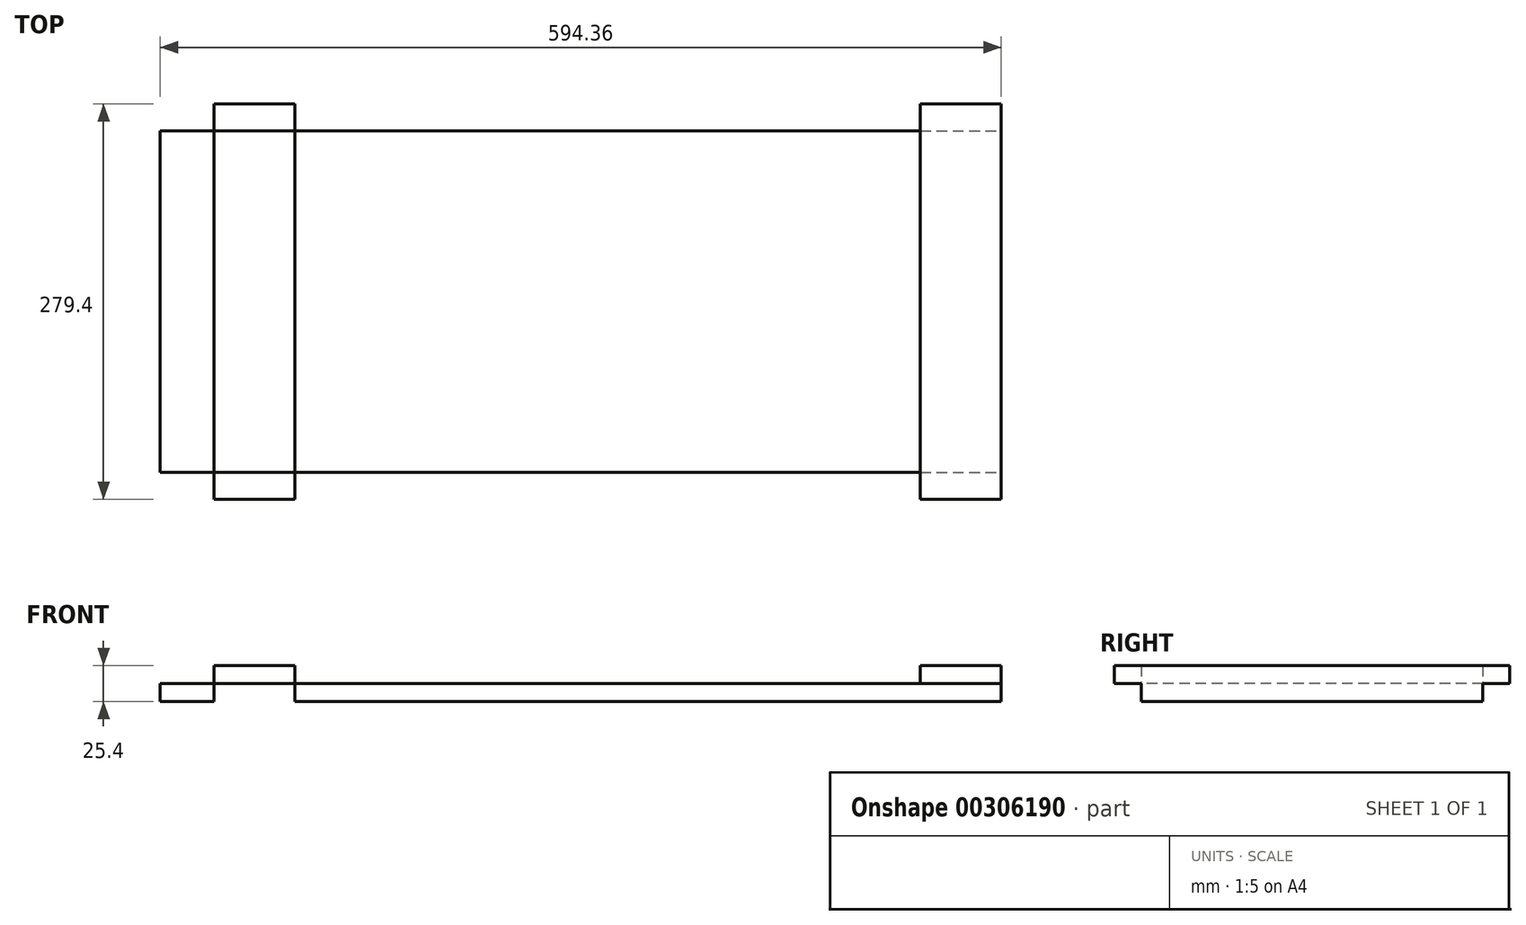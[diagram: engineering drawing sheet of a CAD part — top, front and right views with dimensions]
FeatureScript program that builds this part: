
annotation { "Feature Type Name" : "Feature", "Feature Type Description" : "" }
export const myFeature = defineFeature(function(context is Context, id is Id, definition is map)
    precondition{}
    {
        {
            var Q0;
            Q0=qCreatedBy(makeId("Top.planeOp"),FACE);
            var sketch = newSketch(context, id + "F0", { "sketchPlane" : qUnion([Q0])});
            skLineSegment(sketch, "E0.bottom", {"start": v(-297.18, 120.65) * mm, "end": v(297.18, 120.65) * mm});
            skLineSegment(sketch, "E0.top", {"start": v(-297.18, -120.65) * mm, "end": v(297.18, -120.65) * mm});
            skLineSegment(sketch, "E0.left", {"start": v(-297.18, 120.65) * mm, "end": v(-297.18, -120.65) * mm});
            skLineSegment(sketch, "E0.right", {"start": v(297.18, 120.65) * mm, "end": v(297.18, -120.65) * mm});
            skPoint(sketch, "E0.middle", {"position": v(0, 0) * mm});
            skLineSegment(sketch, "E1.bottom", {"start": v(-259.08, 139.7) * mm, "end": v(-201.93, 139.7) * mm});
            skLineSegment(sketch, "E1.top", {"start": v(-259.08, -139.7) * mm, "end": v(-201.93, -139.7) * mm});
            skLineSegment(sketch, "E1.left", {"start": v(-259.08, 139.7) * mm, "end": v(-259.08, -139.7) * mm});
            skLineSegment(sketch, "E1.right", {"start": v(-201.93, 139.7) * mm, "end": v(-201.93, -139.7) * mm});
            skLineSegment(sketch, "E2", {"start": v(-259.08, 120.65) * mm, "end": v(-201.93, 120.65) * mm});
            skLineSegment(sketch, "E3", {"start": v(-259.08, -120.65) * mm, "end": v(-201.93, -120.65) * mm});
            skLineSegment(sketch, "E4.bottom", {"start": v(297.18, 139.7) * mm, "end": v(240.03, 139.7) * mm});
            skLineSegment(sketch, "E4.top", {"start": v(297.18, -139.7) * mm, "end": v(240.03, -139.7) * mm});
            skLineSegment(sketch, "E4.left", {"start": v(297.18, 139.7) * mm, "end": v(297.18, -139.7) * mm});
            skLineSegment(sketch, "E4.right", {"start": v(240.03, 139.7) * mm, "end": v(240.03, -139.7) * mm});
            skSolve(sketch);
        }
        {
            var Q0;
            {var subQ0=sQuery(id+"F0.wireOp",EDGE,"E0.left");Q0=makeQuery(id+"F0.imprint","IMPRINT",FACE,{"disambiguationData":[TD([[makeQuery(id+"F0.imprint","IMPRINT",EDGE,{"derivedFrom":subQ0}),1.0]])]});}
            var Q1;
            Q1=makeQuery(id+"F0.imprint","IMPRINT",FACE,{"disambiguationData":[TD([[makeQuery(id+"F0.imprint","IMPRINT",EDGE,{"derivedFrom":sQuery(id+"F0.wireOp",EDGE,"ijQMFZE7-lGvI-Rrje-spdO-LlXZxQpasY5D.bottom")}),-1.0]])]});
            var Q2;
            {var subQ2=sQuery(id+"F0.wireOp",EDGE,"ijQMFZE7-lGvI-Rrje-spdO-LlXZxQpasY5D.right");Q2=makeQuery(id+"F0.imprint","IMPRINT",FACE,{"disambiguationData":[TD([[makeQuery(id+"F0.imprint","IMPRINT",EDGE,{"derivedFrom":subQ2}),1.0]])]});}
            var Q3;
            Q3=makeQuery(id+"F0.imprint","IMPRINT",FACE,{"disambiguationData":[TD([[makeQuery(id+"F0.imprint","IMPRINT",EDGE,{"derivedFrom":sQuery(id+"F0.wireOp",EDGE,"27S9jRhR-VNvc-t6gW-FhnJ-kzvBXy7unaTU.bottom")}),1.0]])]});
            var Q4;
            {var subQ0=sQuery(id+"F0.wireOp",EDGE,"E2");Q4=makeQuery(id+"F0.imprint","IMPRINT",FACE,{"disambiguationData":[TD([[makeQuery(id+"F0.imprint","IMPRINT",EDGE,{"derivedFrom":subQ0}),-1.0]])]});}
            var Q5;
            {var subQ0=sQuery(id+"F0.wireOp",EDGE,"27S9jRhR-VNvc-t6gW-FhnJ-kzvBXy7unaTU.right");Q5=makeQuery(id+"F0.imprint","IMPRINT",FACE,{"disambiguationData":[TD([[makeQuery(id+"F0.imprint","IMPRINT",EDGE,{"derivedFrom":subQ0}),-1.0]])]});}
            var Q6;
            {var subQ1=sQuery(id+"F0.wireOp",EDGE,"E0.bottom");var subQ3=sQuery(id+"F0.wireOp",EDGE,"E4.right");var subQ4=makeQuery(id+"F0.imprint","INTERSECT",VERTEX,{"derivedFrom":[subQ1,subQ3]});Q6=makeQuery(id+"F0.imprint","IMPRINT",FACE,{"disambiguationData":[TD([[makeQuery(id+"F0.imprint","IMPRINT",EDGE,{"disambiguationData":[TD([[subQ4,-1.0]])],"derivedFrom":subQ3}),-1.0]])]});}
            var Q7;
            {var subQ0=sQuery(id+"F0.wireOp",EDGE,"E4.left");var subQ1=sQuery(id+"F0.wireOp",EDGE,"E0.bottom");var subQ2=makeQuery(id+"F0.imprint","INTERSECT",VERTEX,{"derivedFrom":[subQ1,subQ0]});Q7=makeQuery(id+"F0.imprint","IMPRINT",FACE,{"disambiguationData":[TD([[makeQuery(id+"F0.imprint","IMPRINT",EDGE,{"disambiguationData":[TD([[subQ2,1.0]])],"derivedFrom":subQ1}),-1.0]])]});}
            extrude(context, id + "F1", {"entities" : qUnion([Q0, Q1, Q2, Q3, Q4, Q5, Q6, Q7]), "oppositeDirection" : true, "depth" : 12.7 * mm});
        }
        {
            var Q0;
            Q0=makeQuery(id+"F0.imprint","IMPRINT",FACE,{"disambiguationData":[TD([[makeQuery(id+"F0.imprint","IMPRINT",EDGE,{"derivedFrom":sQuery(id+"F0.wireOp",EDGE,"ijQMFZE7-lGvI-Rrje-spdO-LlXZxQpasY5D.bottom")}),-1.0]])]});
            var Q1;
            Q1=makeQuery(id+"F0.imprint","IMPRINT",FACE,{"disambiguationData":[TD([[makeQuery(id+"F0.imprint","IMPRINT",EDGE,{"derivedFrom":sQuery(id+"F0.wireOp",EDGE,"27S9jRhR-VNvc-t6gW-FhnJ-kzvBXy7unaTU.bottom")}),1.0]])]});
            var Q2;
            {var subQ0=sQuery(id+"F0.wireOp",EDGE,"E1.bottom");Q2=makeQuery(id+"F0.imprint","IMPRINT",FACE,{"disambiguationData":[TD([[makeQuery(id+"F0.imprint","IMPRINT",EDGE,{"derivedFrom":subQ0}),-1.0]])]});}
            var Q3;
            {var subQ0=sQuery(id+"F0.wireOp",EDGE,"E1.top");Q3=makeQuery(id+"F0.imprint","IMPRINT",FACE,{"disambiguationData":[TD([[makeQuery(id+"F0.imprint","IMPRINT",EDGE,{"derivedFrom":subQ0}),1.0]])]});}
            var Q4;
            {var subQ0=sQuery(id+"F0.wireOp",EDGE,"E2");Q4=makeQuery(id+"F0.imprint","IMPRINT",FACE,{"disambiguationData":[TD([[makeQuery(id+"F0.imprint","IMPRINT",EDGE,{"derivedFrom":subQ0}),-1.0]])]});}
            var Q5;
            {var subQ0=sQuery(id+"F0.wireOp",EDGE,"E4.left");var subQ1=sQuery(id+"F0.wireOp",EDGE,"E0.bottom");var subQ2=makeQuery(id+"F0.imprint","INTERSECT",VERTEX,{"derivedFrom":[subQ1,subQ0]});Q5=makeQuery(id+"F0.imprint","IMPRINT",FACE,{"disambiguationData":[TD([[makeQuery(id+"F0.imprint","IMPRINT",EDGE,{"disambiguationData":[TD([[subQ2,1.0]])],"derivedFrom":subQ1}),-1.0]])]});}
            var Q6;
            {var subQ5=sQuery(id+"F0.wireOp",EDGE,"E4.top");Q6=makeQuery(id+"F0.imprint","IMPRINT",FACE,{"disambiguationData":[TD([[makeQuery(id+"F0.imprint","IMPRINT",EDGE,{"derivedFrom":subQ5}),-1.0]])]});}
            var Q7;
            {var subQ5=sQuery(id+"F0.wireOp",EDGE,"E4.bottom");Q7=makeQuery(id+"F0.imprint","IMPRINT",FACE,{"disambiguationData":[TD([[makeQuery(id+"F0.imprint","IMPRINT",EDGE,{"derivedFrom":subQ5}),1.0]])]});}
            extrude(context, id + "F2", {"entities" : qUnion([Q0, Q1, Q2, Q3, Q4, Q5, Q6, Q7]), "operationType" : NewBodyOperationType.ADD, "depth" : 12.7 * mm});
        }
    });
